# Revit family: Shower-Valve_Trim-KOHLER-Triton-K-TS6913_1
name_source: partatom
category: Specialty Equipment
revit_build: Autodesk Revit 2015 (Build: 20140606_1530(x64)
units: mm (PartAtom-declared; Revit-internal decimal feet)

## types (2) — shared parameters
Assembly Code = C1030200
Date Modified = 03/05/2019
Default Elevation = 42"
Finish = Kohler-Metal-CP-Polished_Chrome
Height = 6 7/16"
Manufacturer = KOHLER Co.
MasterFormat 1995 = 10820
MasterFormat 2004 = 10.28.13
Material = Premium Metal Construction
Product Documentation Link = https://www.us.kohler.com
Product Name = Triton
Product Page URL = http://www.us.kohler.com
URL = https://www.us.kohler.com
WaterSense Certified = No
Width = 6 7/16"

## per-type parameters (varying)
| type | ADA Compliant | Cross_Handle | Description | Distance1 | Handle Clearance | Length | Lever_Handle | Model | Type |
| Cross Handle, CP-Polished Chrome | No | Yes | Rite-Temp valve trim with standard handle | 1 3/8" | 2 3/4" | 2 5/8" | No | K-TS6913-2-CP | 1 |
| Lever Handle, CP-Polished Chrome | Yes | No | Rite-Temp valve trim with lever handle | 0" | 2 7/16" | 3 1/16" | Yes | K-TS6913-4-CP | 2 |

## geometry (parser evidence)
native form markers: Sweep x6
no freeform markers — native parametric forms only
